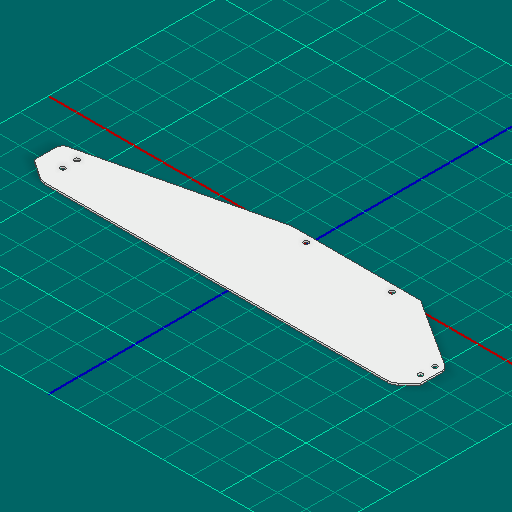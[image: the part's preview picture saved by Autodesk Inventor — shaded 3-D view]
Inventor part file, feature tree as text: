
AUTODESK INVENTOR PART (.ipt)
format: ipt  version: 2025 (Build 290162000, 162)  size: 128,000 bytes
history: native  units: in
note: dims shown in document units (in); Inventor stores cm internally (conversion verified against a paired STEP export)
features: other x3, extrude x1, sketch x1
ambient origin geometry x8: Origin, YZ Plane, XZ Plane, XY Plane, X Axis, Y Axis, Z Axis, Center Point
bodies: Solid1 (feature_tree)
feature tree (5):
  other  "Blocks"
  extrude  "Extrusion1"  Depth=0.0625in TaperAngle=0.0deg
  sketch  "Sketch1"  dims[d0=0.75in d1=0.5in d2=0.75in d3=0.5in d4=0.5in d5=0.75in d6=0.375in d7=0.0625in d8=0.0in]
  other  "main"
  other  "main:1"
